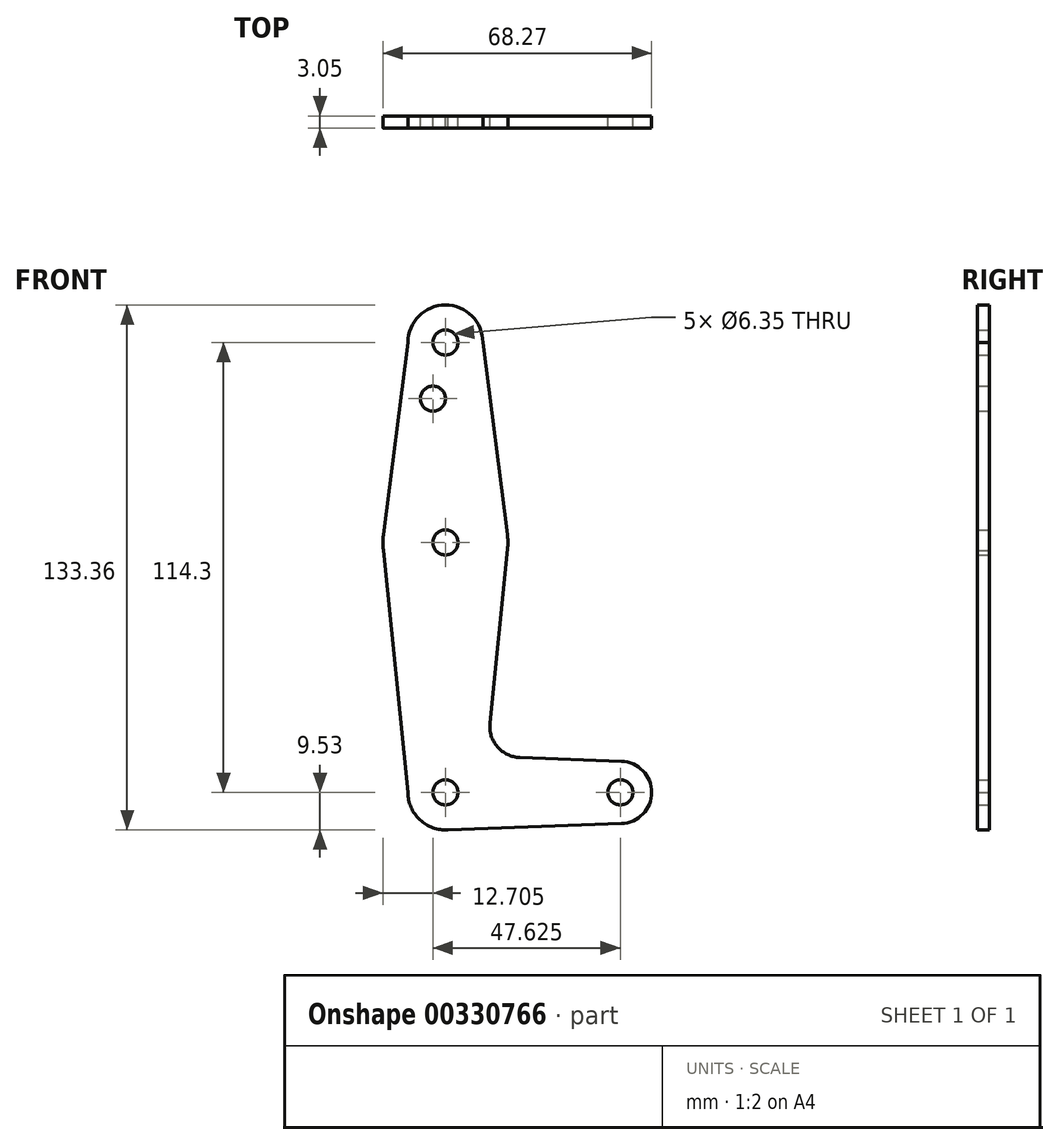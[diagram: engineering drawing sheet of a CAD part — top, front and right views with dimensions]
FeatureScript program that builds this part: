
annotation { "Feature Type Name" : "Feature", "Feature Type Description" : "" }
export const myFeature = defineFeature(function(context is Context, id is Id, definition is map)
    precondition{}
    {
        {
            var Q0;
            Q0=qCreatedBy(makeId("Front.planeOp"),FACE);
            var sketch = newSketch(context, id + "F0", { "sketchPlane" : qUnion([Q0])});
            skLineSegment(sketch, "E0", {"start": v(0, 114.3) * mm, "end": v(0, 0) * mm, "construction": true});
            skLineSegment(sketch, "E1", {"start": v(0, 0) * mm, "end": v(44.45, 0) * mm, "construction": true});
            skCircle(sketch, "E2", {"center": v(0, 114.3) * mm, "radius": 9.53 * mm});
            skCircle(sketch, "E3", {"center": v(44.45, 0) * mm, "radius": 7.94 * mm});
            skCircle(sketch, "E4", {"center": v(0, 63.5) * mm, "radius": 15.88 * mm});
            skCircle(sketch, "E5", {"center": v(0, 0) * mm, "radius": 9.53 * mm});
            skLineSegment(sketch, "E6", {"start": v(-9.53, 114.3) * mm, "end": v(-15.75, 65.5) * mm});
            skLineSegment(sketch, "E7", {"start": v(9.52, 114.3) * mm, "end": v(15.75, 65.5) * mm});
            skLineSegment(sketch, "E8", {"start": v(11.3, 17.6) * mm, "end": v(15.8, 61.9) * mm});
            skLineSegment(sketch, "E9", {"start": v(18.93, 8.85) * mm, "end": v(44.73, 7.93) * mm});
            skLineSegment(sketch, "E10", {"start": v(0, -9.53) * mm, "end": v(44.73, -7.93) * mm});
            skCircle(sketch, "E11", {"center": v(0, 114.3) * mm, "radius": 3.18 * mm});
            skCircle(sketch, "E12", {"center": v(0, 63.5) * mm, "radius": 3.18 * mm});
            skCircle(sketch, "E13", {"center": v(0, 0) * mm, "radius": 3.18 * mm});
            skCircle(sketch, "E14", {"center": v(44.45, 0) * mm, "radius": 3.18 * mm});
            skCircle(sketch, "E15", {"center": v(-3.18, 100.03) * mm, "radius": 3.18 * mm});
            skPoint(sketch, "E16.newPointA", {"position": v(9.53, 0) * mm});
            skArc(sketch, "E16.filletArc", {"start": v(11.3, 17.6) * mm, "mid": v(13.22, 11.57) * mm, "end": v(18.93, 8.85) * mm});
            skLineSegment(sketch, "E17", {"start": v(-15.75, 61.5) * mm, "end": v(-9.53, 0) * mm});
            skSolve(sketch);
        }
        {
            var Q0;
            Q0 = qSketchRegion(id + "F0", true);
            extrude(context, id + "F1", {"entities" : qUnion([Q0]), "depth" : 3.05 * mm});
        }
    });
